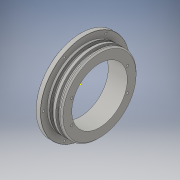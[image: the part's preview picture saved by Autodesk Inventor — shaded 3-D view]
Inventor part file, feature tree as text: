
AUTODESK INVENTOR PART (.ipt)
format: ipt  version: 2016 (Build 200138000, 138)  size: 238,592 bytes
history: native  units: in
note: dims shown in document units (in); Inventor stores cm internally (conversion verified against a paired STEP export)
features: sketch x5, extrude x3, chamfer x2, revolve x1, hole x1
ambient origin geometry x8: Origin, YZ Plane, XZ Plane, XY Plane, X Axis, Y Axis, Z Axis, Center Point
bodies: Solid1 (feature_tree)
feature tree (12):
  revolve  "Revolution1"  [1 undecoded]
  extrude  "Extrusion1"  Depth=0.13in
  extrude  "Extrusion2"  Depth=0.24in
  chamfer  "Chamfer1"  Distance=0.24in
  hole  "Hole1"  [1 undecoded]
  chamfer  "Chamfer2"  Distance=0.125in
  sketch  "Sketch8"  dims[d22=0.139in d23=0.0in d32=0.07in d33=0.125in d34=45.0deg]
  extrude  "Extrusion4"  Depth=0.995in
  sketch  "Sketch2"  dims[d2=0.175in d3=0.14in]
  sketch  "Sketch3"  dims[d4=0.175in d5=0.13in]
  sketch  "Sketch5"  dims[d8=90.0deg d10=4.65in d11=0.24in d12=0.0in]
  sketch  "Sketch9"  dims[d38=0.5in d42=0.125in d43=4.35in d44=2.3622in d46=360.0deg d48=0.1181in d49=0.75in d50=0.375in d51=0.25in d52=0.5635in d53=1.0in d54=0.8108in d55=0.01in d56=0.125in d57=45.0deg d62=3.819in d65=0.15in d66=0.15in d67=0.15in d68=0.055in d71=0.755in d72=1.68in d73=0.3in d74=0.3in d78=0.1181in d79=0.1181in d83=0.1181in d84=0.1181in d85=0.995in d86=0.0in]
note: 2 required parameter values undecoded (feature->parameter linkage not recoverable at this tier; creation-order binding heuristic only, values carry confidence <= 0.55)